FCSTD DOCUMENT  (FreeCAD 1.0R39109 (Git))
Label: Master Document
License: All rights reserved
LicenseURL: http://en.wikipedia.org/wiki/All_rights_reserved
objects: Spreadsheet::Sheet×1

FEATURE [Spreadsheet::Sheet] Spreadsheet  label="Monitor Chassis Parameters"
  cells = A1='Parameter Name; B1='Value; C1='Notes; A2='GSWallHalfLength; B2(GSWallHalfLength)==B51; C2='Does not include outer radius portion of the wall, only the rectangular part; A3='GSBottomWallHeight; B3(GSBottomWallHeight)==B81 + B98 + B11; A4='GSWallWidth; B4(GSWallWidth)=123; A5='GSBaseFloorBeamWidth; B5(GSBaseFloorBeamWidth)==B33 * 3; C5='Is relelative to the size of the screw hole size; A6='GSBaseBodyThickness; B6(GSBaseBodyThickness)=3; A7='GSCamWallThickness; B7(GSCamWallThickness)=4; A8='GSThinWallThickness; B8(GSThinWallThickness)=3; A9='GSCamWallClickIndent; B9(GSCamWallClickIndent)=1; A10='GSCamWallClickLength; B10(GSCamWallClickLength)=6; A11='GSCamWallFullClickStructureHeight; B11(GSCamWallFullClickStructureHeight)=20; A14='GSCamBoardHeight; B14(GSCamBoardHeight)=38; A15='GSCamBoardWidth; B15(GSCamBoardWidth)=38; A16='GSCamBoardMountingHoleDiameter; B16(GSCamBoardMountingHoleDiameter)==B42; A17='GSCamPlateThickness; B17(GSCamPlateThickness)=4; A18='GSCamMountingHoleOffset; B18(GSCamMountingHoleOffset)=4; A19='GSCamMountingHoleThickness; B19(GSCamMountingHoleThickness)=2; A20='GSCamMountingHoleHeight; B20(GSCamMountingHoleHeight)=7; A21='GSCamAxisHoleDiameter; B21(GSCamAxisHoleDiameter)==B43; C21='M4 uses a 4.5 mm hole; A22='GSCamAxisWidth; B22(GSCamAxisWidth)=22; A23='GSCamMountingIndentInnerDiameter; B23(GSCamMountingIndentInnerDiameter)=5; C23='TBD - Not a good name?; A24='GSCamMountingHoleDiameter; B24(GSCamMountingHoleDiameter)=2.5; A25='GSCamGimbalDepth; B25(GSCamGimbalDepth)=20; A26='GSCam1ZAxisSetback; B26(GSCam1ZAxisSetback)=15; C26='The camera will be mounted back, away from the lens to help the tilt ability; A27='GSCam2ZAxisSetback; B27(GSCam2ZAxisSetback)=15; C27='The camera will be mounted back, away from the lens to help the tilt ability; A28='GSCamGimbalLighteningSlotOffsetFromCenter; B28(GSCamGimbalLighteningSlotOffsetFromCenter)=12; A29='GSCamGimbalInnerLength; B29(GSCamGimbalInnerLength)=58; A30='GSCam1GimbalHoleHeight; B30(GSCam1GimbalHoleHeight)=50; A31='GSCam2GimbalHoleHeight; B31(GSCam2GimbalHoleHeight)=35; A32='GSCamM4NutHexagonDiameter; B32(GSCamM4NutHexagonDiameter)=8.4; A33='GSCamM4ScrewHoleDiameter; B33(GSCamM4ScrewHoleDiameter)=3.3; A34='GSCamM4NutDepth; B34(GSCamM4SNutDepth)=4; A35='GSCamM3NutDepth; B35(GSCamM3NutDepth)=3.5; A36='GSCamM5NutHexagonDiameter; B36(GSCamM5NutHexagonDiameter)=9.5; A37='GSCamM3NutHexagonDiameter; B37(GSCamM3NutHexagonDiameter)=6.6; A38='GSCamM5ScrewHoleDiameter; B38(GSCamM5ScrewHoleDiameter)=5.5; A39='GSCamM5NutDepth; B39(GSCamM5NutDepth)=4; A40='GSLEDPowerRiserHeight; B40(GSLEDPowerRiserHeight)=7; A41='GSM3BoltHoleDiameter; B41(GSM3BoltHoleDiameter)=3.4; A42='GSM25BoltHoleDiameter; B42(GSM25BoltHoleDiameter)=2.9; A43='GSM4BoltHoleDiameter; B43(GSM4BoltHoleDiameter)=4.5; A44='GSM4BoltHeadIndentDiameter; B44(GSM4BoltHeadIndentDiameter)=7.5; A46='GSM3TappingScrewHoleDiameter; B46(GSM3TappingScrewHoleDiameter)=2.4; A48='GSMonitorFloorPowerBayLength; B48(GSMonitorFloorPowerBayLength)=155; A50='GSMonitorFloorWidth_PiSide; B50(GSMonitorFloorWidth_PiSide)==B4 - 2 * B8; A51='GSMonitorFloorLength_PiSide; B51(GSMonitorFloorLength_PiSide)=170; A52='GSMonitorCameraBayLength; B52(GSMonitorCameraBayLength)=130; C52='TBD - May not use.  Instead, just have a single right- and left- number so that the viewports are the same?; F52='Total Inner Length; G52==B52 + B57 + B58 + B68; A53='GSMonitorStrobeBayLength; B53(GSMonitorStrobeBayLength)=130; C53='TBD - Not used; A54='GSMonitorViewPortLengthRight; B54(GSMonitorViewPortLengthRight)=100; A55='GSMonitorViewPortLengthLeft; B55(GSMonitorViewPortLengthLeft)=50; A57='GSMonitorPiBayLength; B57(GSMonitorPiBayLength)=100; A58='GSMonitorExtraBayLength; B58(GSMonitorExtraBayLength)=10; A59='GSMonitorFloorThickness; B59(GSMonitorFloorThickness)=4; A60='GSMonitorFloorPiSideLengthShare; B60(GSMonitorFloorPiSideLengthShare)=30; C60='This amount of the Pi-side is moved to the Power side to share the overall length to fit on printer; A61='GSMonitorFloorJointOverlap; B61(GSMonitorFloorJointOverlap)=14; A62='GSMonitorFloorPiEndOffset; B62(GSMonitorFloorPiEndOffset)=32; C62='Offset from end of floor rectangle (not rounded part) to nearest Pi board mounting hole; A63='GSMonitorFloorPiNearSideOffset; B63(GSMonitorFloorPiNearSideOffset)=51; C63='Offset from camera side of inner wall to the Pi 5 mounting screw; A64='GSMonitorFloorMountHoleSideOffset; B64(GSMonitorFloorMountHoleSideOffset)=8; C64='From inner side to the hole that the floor will be screwed into; A65='GSMonitorFloorMountHoleSideOffsetForWall; B65(GSMonitorFloorMountHoleSideOffsetForWall)==B64 - 1; C65='TBD - Fix so that a separate value here is not needed.  Needed because wall measures the side offset from the lip, not the  same place the Floor does.; A66='GSM5ScrewHoleDiameter; B66(GSM5ScrewHoleDiameter)=3.3; A67='GSMonitorFloorMountHoleEdgeOffset; B67(GSMonitorFloorMountHoleEdgeOffset)=8; C67='From edge (e.g., from the side or the middle of the floors) back to the screw that will mount to the wall; A68='GSMonitorFloorPowerBayLength; B68=150; A69='GSMonitorFloorMountingScrewDiameter; B69(GSMonitorFloorMountingScrewDiameter)=2.5; C69='2.4 is nominal, but that was a little tight in PLA; A70='GSMonitorFloorRibMinimumWidth; B70(GSMonitorFloorRibMinimumWidth)=10; A71='GSMonitorFloorMountingScrewDepth; B71(GSMonitorFloorMountingScrewDepth)=6; A72='GSMonitorWallTensionReliefCutWidth; B72(GSMonitorWallTensionReliefCutWidth)=0.5; A73='GSMonitorWallHalfConnectionBoltDiameter; B73(GSMonitorWallHalfConnectionBoltDiameter)==B41; A74='GSMonitorPowerFloorJointScrewEdgeOffset; B74(GSMonitorPowerFloorJointScrewEdgeOffset)=8; A76='GSPi5MountingHoleCenterLength; B76(GSPi5MountingHoleCenterLength)=58; A77='GsPi5MountingHoleCenterWidth; B77(GSPi5MountingHoleCenterWidth)=49; A78='GsPi5MountingHoleDiameter; B78(GsPi5MountingHoleDiameter)=3; A79='GsPi5NetworkSideBoardLength; B79(GsPi5NetworkSideBoardLength)=22; C79='Length from the edge of the nearest mounting hole to the side of the board that has the network connector on it; A80='GSPi5MountingRiserHeight; B80(GSPi5MountingRiserHeight)=4; A81='GSPi5FullHeightInclConnectorsAndFloor; B81(GSPi5FullHeightInclConnectorsAndFloor)=60; A83='GSMonitorFloorCameraMountHoleDiameter; B83(GSMonitorFloorCameraMountHoleDiameter)==B38; A84='GSMonitorFloorCamera1_MountHoleFrontOffset; B84(GSMonitorFloorCamera1_MountHoleFrontOffset)=56; C84='Critical, as must be far enough back to avoid lense hitting front of enclosure, but close enough to allow good down-angling; A85='GSMonitorFloorCamera2_MountHoleFrontOffset; B85(GSMonitorFloorCamera2_MountHoleFrontOffset)=50; A86='GSMonitorFloorCameraMountHoleEdgeOffset; B86(GSMonitorFloorCameraMountHoleEdgeOffset)=155; C86='Offset from outer (right) edge - TBD - is this in use?; A87='GSMonitorFloorCamera1MountHoleEdgeOffsetFromCenter; B87(GSMonitorFloorCamera1MountHoleEdgeOffsetFromCenter)=23; C87='TBD - Need smaller gimbal dimensions to make this fit; A88='GSMonitorFloorCamera2MountHoleEdgeOffsetFromCenter; B88(GSMonitorFloorCamera2MountHoleEdgeOffsetFromCenter)=25; A90='GSMonitorFloorStrobeMountHoleDiameter; B90(GSMonitorFloorStrobeMountHoleDiameter)==B38; A91='GSMonitorFloorStrobeMountHoleFrontOffset; B91(GSMonitorFloorStrobeMountHoleFrontOffset)=30; A92='GSMonitorFloorStrobeMountHoleEdgeOffset; B92(GSMonitorFloorStrobeMountHoleEdgeOffset)=45; A95='GSLEDDriverMountingHoleWidth; B95(GSLEDDriverMountingHoleWidth)=43; A96='GSLEDDriverMountingHoleLength; B96(GSLEDDriverMountingHoleLength)=127; A98='GSMonitorFloorOffsetFromBottom; B98(GSMonitorFloorOffsetFromBottom)=60; C98='For the two-floored layer, the offset from the bottom of the wall to the top of the floor; A99='GSMiddleTopFloorDistanceFromBottom; B99(GSMiddleTopFloorDistanceFromBottom)==GSLEDViewPortBottomHeight + GsMonitorWall2InterFloorSeparation; C99='Distance from the bottom of the middle wall to the bottom of where the top floor sits in that middle section; A100='GSMiddleBottomFloorPadDistanceFromBottom; B100(GSMiddleBottomFloorPadDistanceFromBottom)=20; +152 more cells
